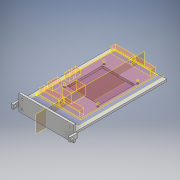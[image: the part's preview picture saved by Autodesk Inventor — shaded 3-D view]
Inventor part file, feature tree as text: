
AUTODESK INVENTOR PART (.ipt)
format: ipt  version: 2018 (Build 220112000, 112)  size: 258,048 bytes
history: native  units: mm
features: sketch x6, other x4, extrude x4, plane x2, mirror x1
ambient origin geometry x8: Origin, YZ Plane, XZ Plane, XY Plane, X Axis, Y Axis, Z Axis, Center Point
bodies: Solid1 (feature_tree)
feature tree (17):
  other  "PCB.ipt"
  plane  "Work Plane1"
  sketch  "Sketch3"  dims[d2=5.0mm d3=5.0mm d4=133.0mm]
  extrude  "Extrusion1"  Depth=3.0mm
  extrude  "Extrusion2"  Depth=133.0mm
  extrude  "Extrusion3"  Depth=3.0mm TaperAngle=0.0deg
  extrude  "Extrusion4"  Depth=80.0mm
  plane  "Work Plane2"
  mirror  "Mirror1"
  other  "TaggingFeature1"
  sketch  "Sketch2"  dims[d0=10.0mm d1=3.0mm]
  sketch  "Sketch4"  dims[d5=113.0mm d6=3.0mm d7=0.0mm]
  sketch  "Sketch5"  dims[d8=80.0mm d9=80.0mm]
  sketch  "Sketch6"  dims[d10=10.0mm]
  sketch  "Sketch7"  dims[d11=10.0mm d12=5.0mm d13=2.7mm d14=5.0mm d15=5.0mm d16=5.0mm d17=3.0mm d18=3.0mm d19=0.0mm d20=16.152434mm d21=16.152434mm d22=30.0mm d24=133.0mm d25=51.5mm d26=10.0mm d27=0.0mm d28=80.0mm d29=6.0mm d30=11.0mm d31=3.0mm d32=23.0mm d33=6.5mm d34=3.2mm d35=3.0mm d36=3.0mm d37=0.0mm]
  other  "Solid1::PCB.ipt"
  other  "Srf1"
